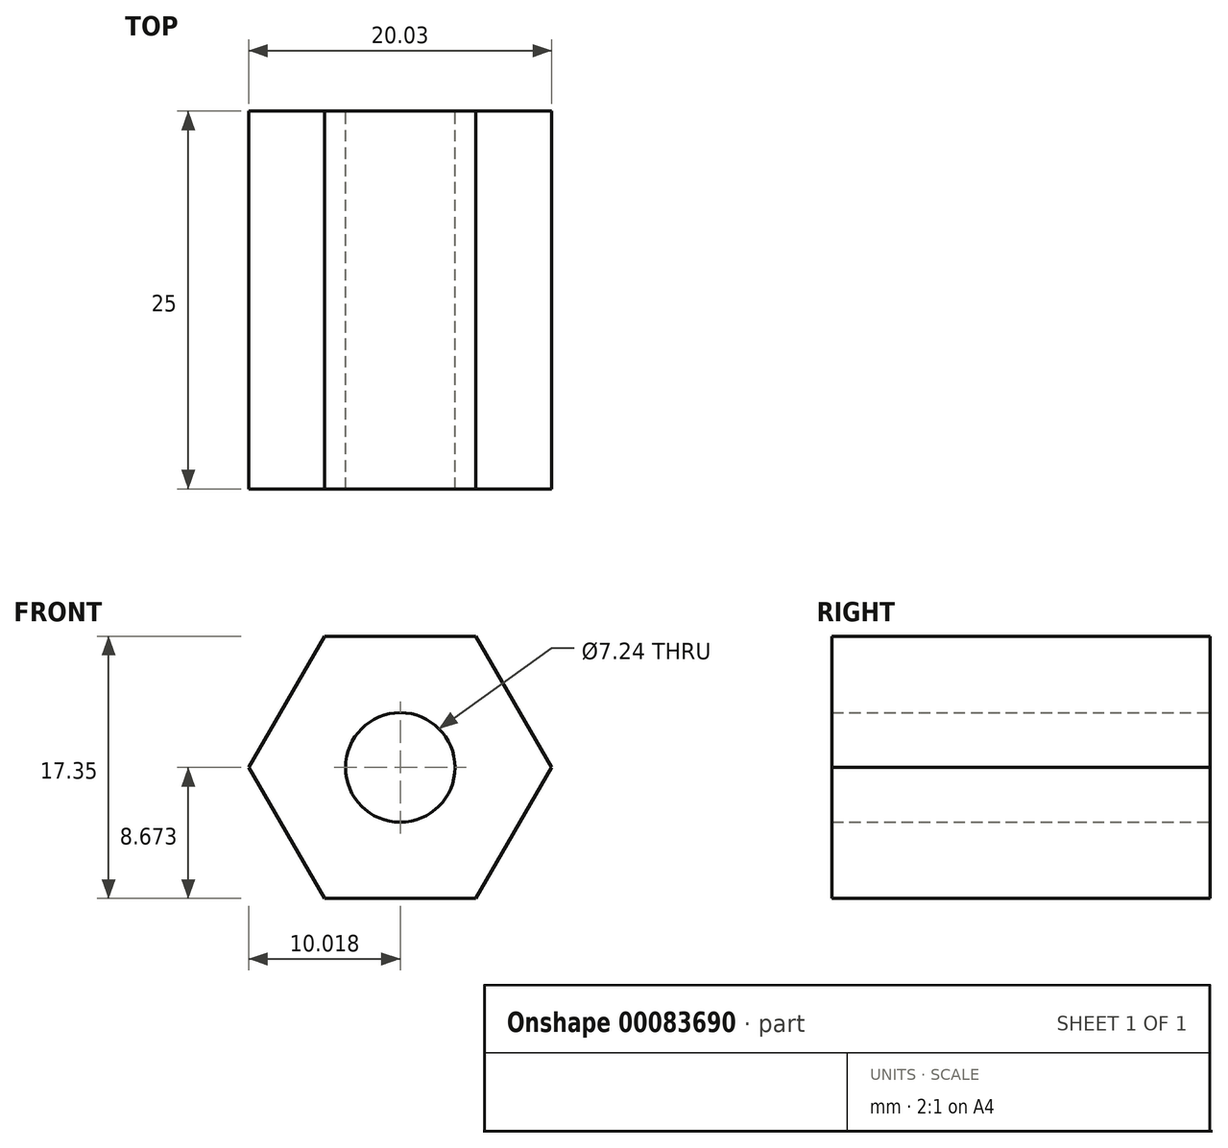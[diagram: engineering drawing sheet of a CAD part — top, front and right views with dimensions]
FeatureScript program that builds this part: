
annotation { "Feature Type Name" : "Feature", "Feature Type Description" : "" }
export const myFeature = defineFeature(function(context is Context, id is Id, definition is map)
    precondition{}
    {
        {
            var Q0;
            Q0=qCreatedBy(makeId("Front.planeOp"),FACE);
            var sketch = newSketch(context, id + "F0", { "sketchPlane" : qUnion([Q0])});
            skCircle(sketch, "E0", {"center": v(-29.3, 23.42) * mm, "radius": 3.62 * mm});
            skCircle(sketch, "E1.cCircle", {"center": v(-29.3, 23.42) * mm, "radius": 8.68 * mm, "construction": true});
            skLineSegment(sketch, "E1.0", {"start": v(-34.31, 32.1) * mm, "end": v(-24.3, 32.1) * mm});
            skLineSegment(sketch, "E1.1", {"start": v(-24.3, 32.1) * mm, "end": v(-19.29, 23.42) * mm});
            skLineSegment(sketch, "E1.2", {"start": v(-19.29, 23.42) * mm, "end": v(-24.3, 14.75) * mm});
            skLineSegment(sketch, "E1.3", {"start": v(-24.3, 14.75) * mm, "end": v(-34.31, 14.75) * mm});
            skLineSegment(sketch, "E1.4", {"start": v(-34.31, 14.75) * mm, "end": v(-39.32, 23.42) * mm});
            skLineSegment(sketch, "E1.5", {"start": v(-39.32, 23.42) * mm, "end": v(-34.31, 32.1) * mm});
            skPoint(sketch, "E1.0.midPoint", {"position": v(-29.3, 32.1) * mm});
            skSolve(sketch);
        }
        {
            var Q0;
            Q0=makeQuery(id+"F0.imprint","IMPRINT",FACE,{"disambiguationData":[TD([[makeQuery(id+"F0.imprint","IMPRINT",EDGE,{"derivedFrom":sQuery(id+"F0.wireOp",EDGE,"E0")}),-1.0]])]});
            var Q1;
            Q1=makeQuery(id+"F0.imprint","IMPRINT",FACE,{"disambiguationData":[TD([[makeQuery(id+"F0.imprint","IMPRINT",EDGE,{"derivedFrom":sQuery(id+"F0.wireOp",EDGE,"E0")}),1.0]])]});
            extrude(context, id + "F1", {"entities" : qUnion([Q0, Q1]), "depth" : 25 * mm});
        }
        {
            var Q0;
            Q0=makeQuery(id+"F0.imprint","IMPRINT",FACE,{"disambiguationData":[TD([[makeQuery(id+"F0.imprint","IMPRINT",EDGE,{"derivedFrom":sQuery(id+"F0.wireOp",EDGE,"E0")}),1.0]])]});
            var Q1;
            Q1=sQuery(id+"F0.wireOp",EDGE,"E0");
            extrude(context, id + "F2", {"entities" : qUnion([Q0]), "operationType" : NewBodyOperationType.REMOVE, "surfaceEntities" : qUnion([Q1]), "depth" : 25 * mm});
        }
    });
